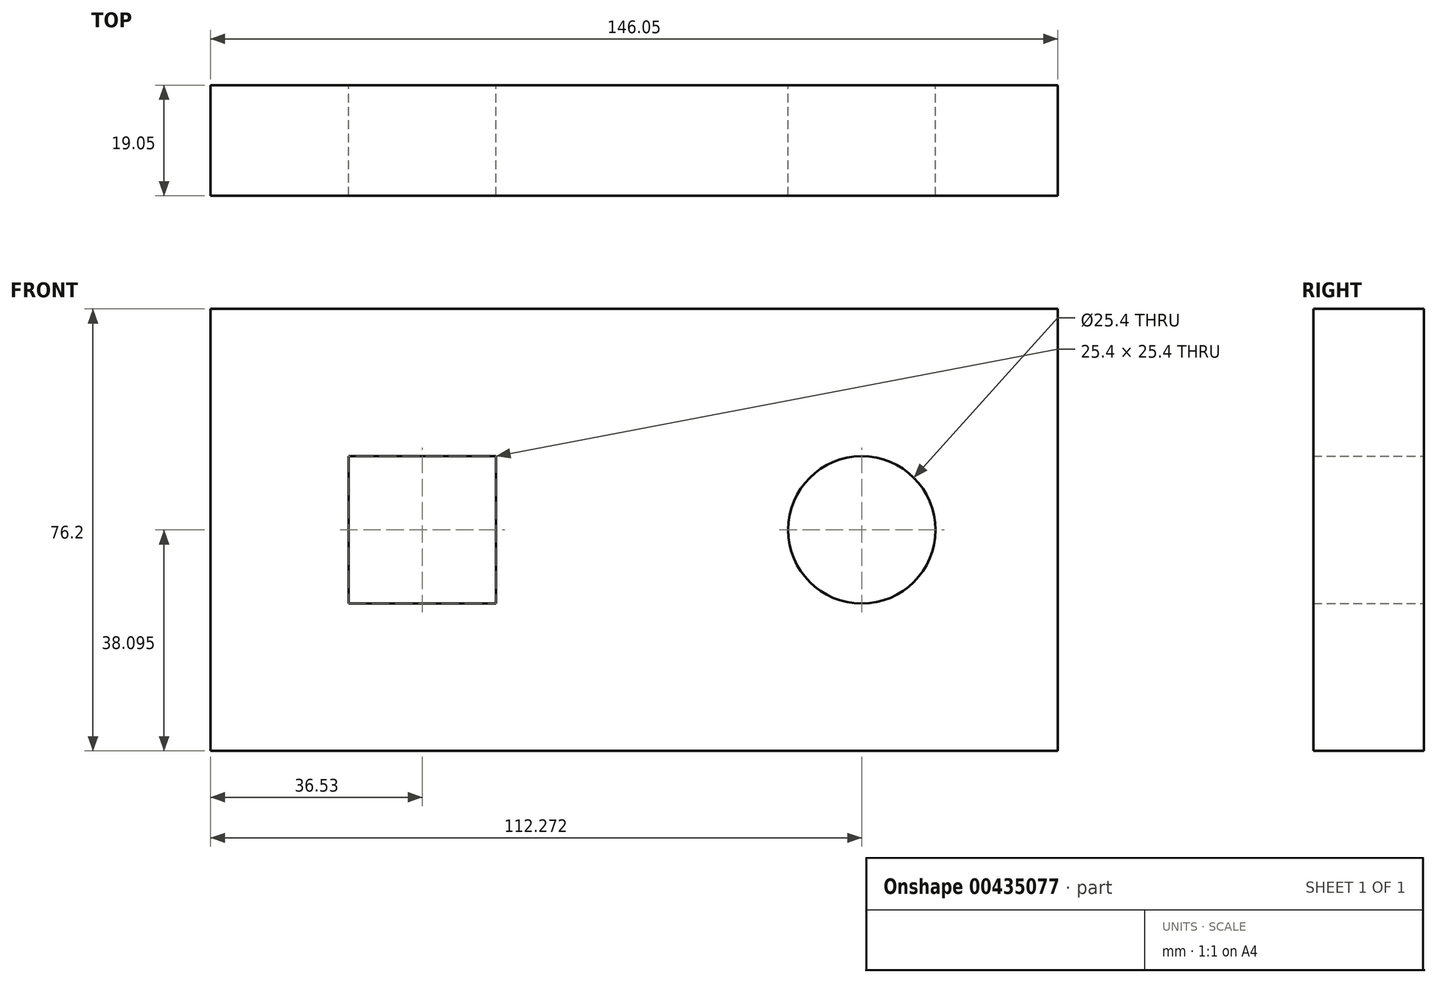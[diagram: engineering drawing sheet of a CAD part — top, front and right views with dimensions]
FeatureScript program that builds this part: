
annotation { "Feature Type Name" : "Feature", "Feature Type Description" : "" }
export const myFeature = defineFeature(function(context is Context, id is Id, definition is map)
    precondition{}
    {
        {
            var Q0;
            Q0=qCreatedBy(makeId("Front.planeOp"),FACE);
            var sketch = newSketch(context, id + "F0", { "sketchPlane" : qUnion([Q0])});
            skLineSegment(sketch, "E0", {"start": v(-73.65, 54.6) * mm, "end": v(-73.65, -21.6) * mm});
            skLineSegment(sketch, "E1", {"start": v(-73.65, -21.6) * mm, "end": v(72.4, -21.6) * mm});
            skLineSegment(sketch, "E2", {"start": v(72.4, -21.6) * mm, "end": v(72.4, 54.6) * mm});
            skLineSegment(sketch, "E3", {"start": v(72.4, 54.6) * mm, "end": v(-73.65, 54.6) * mm});
            skLineSegment(sketch, "E4.bottom", {"start": v(-49.82, 29.2) * mm, "end": v(-24.42, 29.2) * mm});
            skLineSegment(sketch, "E4.top", {"start": v(-49.82, 3.8) * mm, "end": v(-24.42, 3.8) * mm});
            skLineSegment(sketch, "E4.left", {"start": v(-49.82, 29.2) * mm, "end": v(-49.82, 3.8) * mm});
            skLineSegment(sketch, "E4.right", {"start": v(-24.42, 29.2) * mm, "end": v(-24.42, 3.8) * mm});
            skCircle(sketch, "E5", {"center": v(38.62, 16.5) * mm, "radius": 12.7 * mm});
            skSolve(sketch);
        }
        {
            var Q0;
            Q0 = qSketchRegion(id + "F0", true);
            extrude(context, id + "F1", {"entities" : qUnion([Q0]), "depth" : 19.05 * mm});
        }
    });
